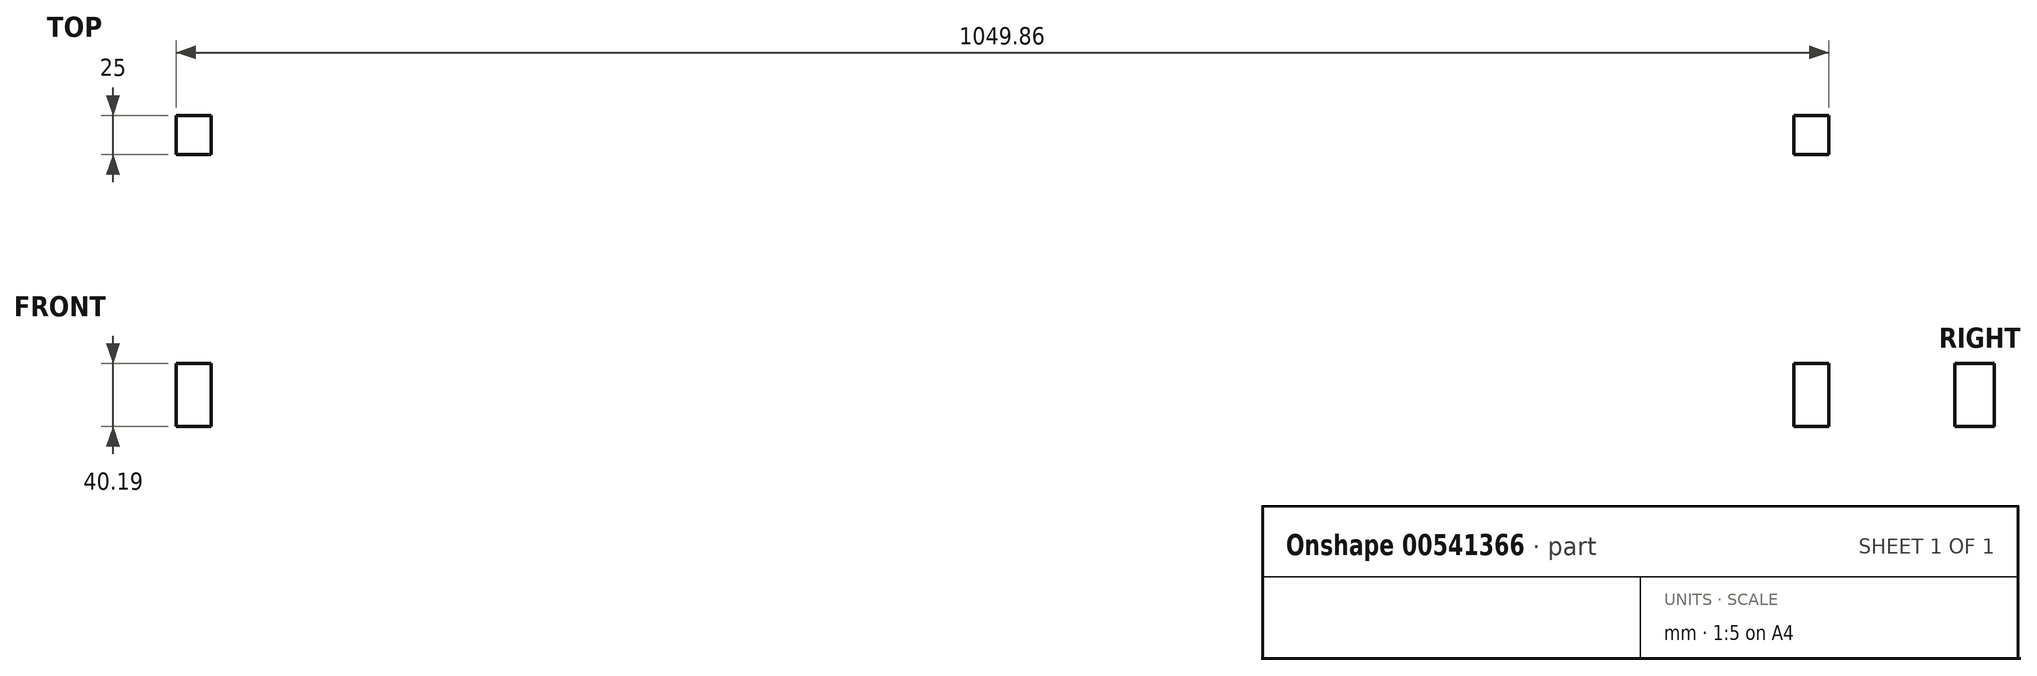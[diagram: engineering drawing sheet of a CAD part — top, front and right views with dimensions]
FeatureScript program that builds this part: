
annotation { "Feature Type Name" : "Feature", "Feature Type Description" : "" }
export const myFeature = defineFeature(function(context is Context, id is Id, definition is map)
    precondition{}
    {
        {
            var Q0;
            Q0=qCreatedBy(makeId("Front.planeOp"),FACE);
            var sketch = newSketch(context, id + "F0", { "sketchPlane" : qUnion([Q0])});
            skLineSegment(sketch, "E0", {"start": v(-66.36, 0) * mm, "end": v(-66.36, 40.2) * mm});
            skLineSegment(sketch, "E1", {"start": v(-66.36, 40.2) * mm, "end": v(-43.93, 40.2) * mm});
            skLineSegment(sketch, "E2", {"start": v(-43.93, 40.2) * mm, "end": v(-43.93, 0) * mm});
            skLineSegment(sketch, "E3", {"start": v(-43.93, 0) * mm, "end": v(-66.36, 0) * mm});
            skSolve(sketch);
        }
        {
            var Q0;
            Q0 = qSketchRegion(id + "F0", true);
            extrude(context, id + "F1", {"entities" : qUnion([Q0]), "depth" : 25 * mm, "offsetDistance" : 25 * mm});
        }
        {
            var Q0;
            Q0=qCreatedBy(makeId("Front.planeOp"),FACE);
            var sketch = newSketch(context, id + "F2", { "sketchPlane" : qUnion([Q0])});
            skLineSegment(sketch, "E4", {"start": v(961.07, 0) * mm, "end": v(961.07, 40.19) * mm});
            skLineSegment(sketch, "E5", {"start": v(961.07, 40.19) * mm, "end": v(983.5, 40.19) * mm});
            skLineSegment(sketch, "E6", {"start": v(983.5, 40.19) * mm, "end": v(983.5, 0) * mm});
            skLineSegment(sketch, "E7", {"start": v(983.5, 0) * mm, "end": v(961.07, 0) * mm});
            skSolve(sketch);
        }
        {
            var Q0;
            Q0 = qSketchRegion(id + "F2", true);
            extrude(context, id + "F3", {"entities" : qUnion([Q0]), "depth" : 25 * mm, "offsetDistance" : 25 * mm});
        }
    });
